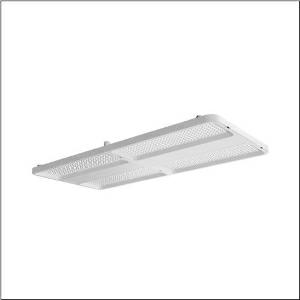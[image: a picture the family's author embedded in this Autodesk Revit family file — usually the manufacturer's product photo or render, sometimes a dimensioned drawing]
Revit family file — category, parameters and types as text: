
# Revit family: highbay_21_maxi_52hn11db4rda
name_source: partatom
category: Lighting Fixtures
units: mm (PartAtom-declared; Revit-internal decimal feet)

## family parameters
Cut with Voids When Loaded = No
Host = Face
Light Source = No
Part Type = Normal
Room Calculation Point = No
Round Connector Dimension = Use Diameter
Shared = No

## types (1)
- --- (1 x LED, 7000 lm, 38.3 W, 4000K)
    Apparent Load = 38 VA
    CIE Flux Codes = 89 97 99 100 100
    Color Rendering = 80
    Color Temperature = 4000K
    Default Elevation = 1800 mm
    Description = high bay luminaire Highbay 21 maxi; direct symmetric narrow distribution, light control with lens of PMMA; UGR ≤ 22 (X = 4H | Y = 8H | S = 0.25H | reflection values 70/50/20); luminous flux: 45.000lm; light colour: 840, colour temperature: 4000K, MacAdam ≤ 3 SDCM (initial), colour rendering: CRI > 80; luminous efficacy: 188lm/W; rated service life: 75.000h (L80/B50) at AT= ta max; control: DALI 2; housing frame of high-performance plastic PA6, matt traffic white (RAL 9016); cover of PMMA; dimension (LxWxH): 946 x 442 x 72mm; luminaire connection: terminal, 5-pole, max. 2.5mm² (cable entry for one cable, Ø 8.5..16mm); mains connection: 230..240V, AC/DC 0/50..60Hz; connected load: 239,3W; protection rating (complete): IP66; insulation class (complete): insulation class I (protective earthing); protection symbol: D; impact resistance: IK08; halogen-free wiring; for central battery installations according to DIN EN 60598-2-22; LABS conformity tested according to VDMA 24364:2018-05; corresponds to IFS (International Featured Standards) requirements for safety and quality in the food industry; certification: CE, ENEC, VDE, UKCA; permissible operating ambient temperature: -40..+55°C (reducing of maximum allowable ambient temperature of 5°C with ceiling mounting); packaging unit: 1 piece; (delivery without accessories; please order mounting accessories separately)
    Height = 72 mm  [stored 0.23622 ft]
    Lamp = 1 x LED
    Lamp Light Flux = 7000 lm
    Lamp Power = 38.3 W
    Lamp count = 1
    Length = 946 mm
    Luminous efficacy = 183 lm/W
    Manufacturer = Siteco
    ModVariant = No
    Model = 52HN11DB4RDA
    Mounting Place = Ceiling
    Mounting Type = Pendant
    Number of Poles = 1
    OnlyDefault = Yes
    Power Factor = 1
    Product Name = Highbay 21 maxi
    Product group = high bay luminaire
    ProductGroupID = 901
    Protection Class = Protection class I
    Protection Degree = IP 66
    RLX_Detail_Level = 1
    RLX_Emergency_Light_Flux = 0 lm
    RLX_Emergency_Type = 0
    RLX_Emergency_Type_DB = No
    RlxData = <blob elided: 23149 chars, md5=7287c842>
    Socket = socket
    Standby Power = 0 W
    System Light Flux = 7000 lm
    System Power = 38 W
    Type Comments = : DC mode (central or group accumulator) initial emergency light level
    Type Image = l_1363244.jpg
    URL = http://relux.com
    VarID = @adj_000169
    Voltage = 0 V
    Weight = 0.00 kg
    Width = 442 mm

note: [stored X ft] marks values corroborated as IEEE doubles in the binary element streams (Revit-internal decimal feet)

## geometry (parser evidence)
native form markers: Blend x4, Sweep x10
no freeform markers — native parametric forms only
